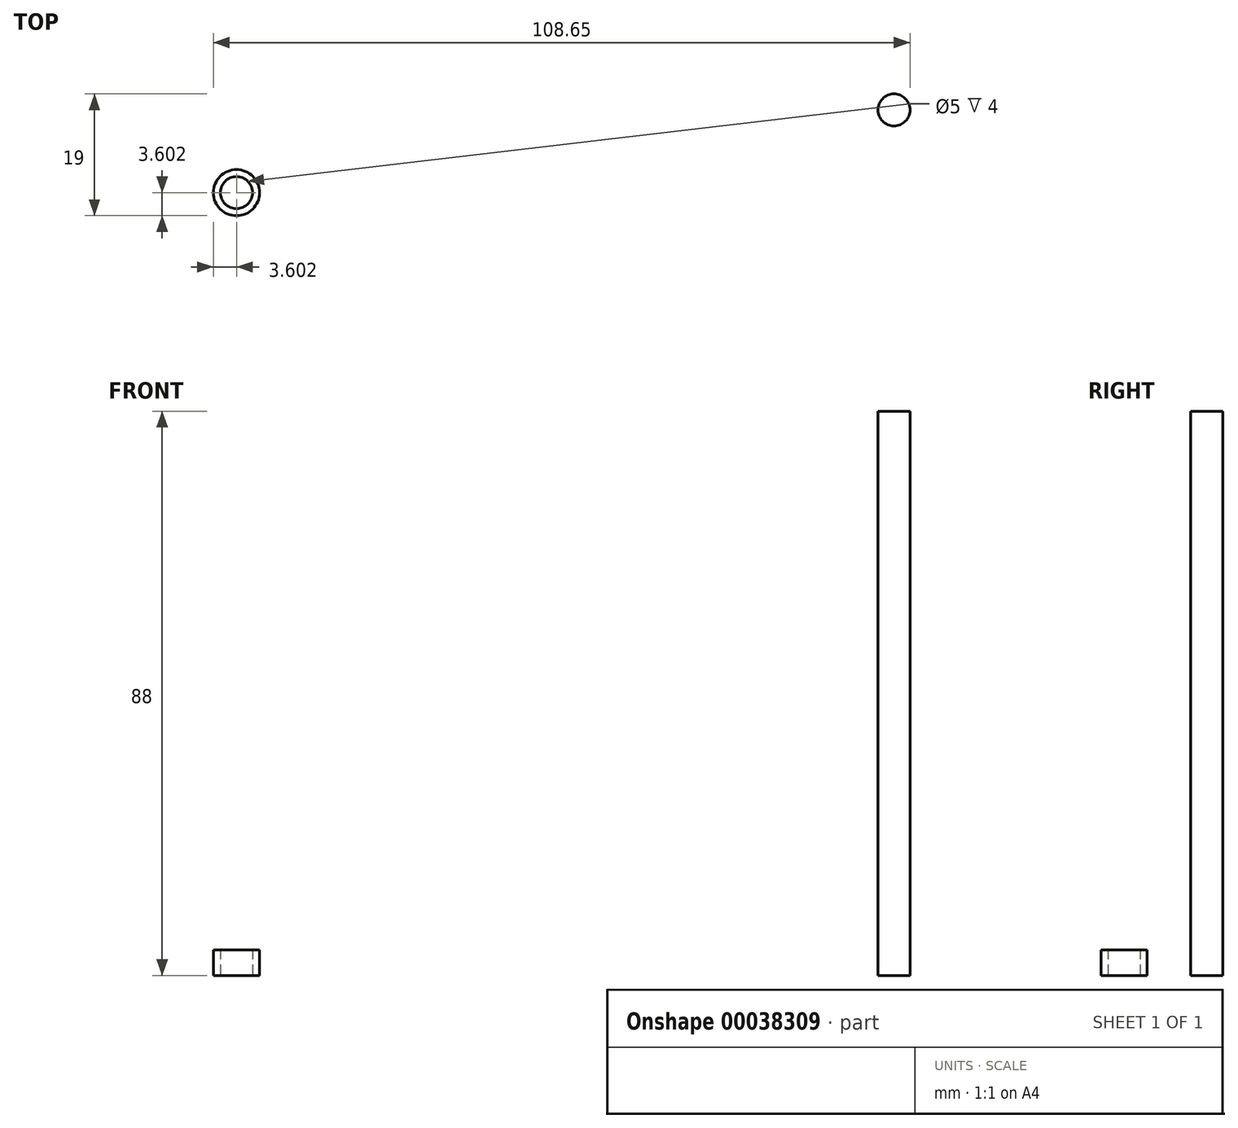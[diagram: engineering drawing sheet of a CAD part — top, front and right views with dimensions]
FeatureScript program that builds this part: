
annotation { "Feature Type Name" : "Feature", "Feature Type Description" : "" }
export const myFeature = defineFeature(function(context is Context, id is Id, definition is map)
    precondition{}
    {
        {
            var Q0;
            Q0=qCreatedBy(makeId("Top.planeOp"),FACE);
            var sketch = newSketch(context, id + "F0", { "sketchPlane" : qUnion([Q0])});
            skCircle(sketch, "E0", {"center": v(0, 0) * mm, "radius": 2.5 * mm});
            skSolve(sketch);
        }
        {
            var Q0;
            Q0 = qSketchRegion(id + "F0", true);
            extrude(context, id + "F1", {"entities" : qUnion([Q0]), "depth" : 88 * mm});
        }
        {
            var Q0;
            Q0=qCreatedBy(makeId("Top.planeOp"),FACE);
            var sketch = newSketch(context, id + "F2", { "sketchPlane" : qUnion([Q0])});
            skCircle(sketch, "E1", {"center": v(-102.55, -12.9) * mm, "radius": 3.6 * mm});
            skCircle(sketch, "E2", {"center": v(-102.55, -12.9) * mm, "radius": 2.5 * mm});
            skSolve(sketch);
        }
        {
            var Q0;
            Q0 = qSketchRegion(id + "F2", true);
            extrude(context, id + "F3", {"entities" : qUnion([Q0]), "depth" : 4 * mm});
        }
    });
